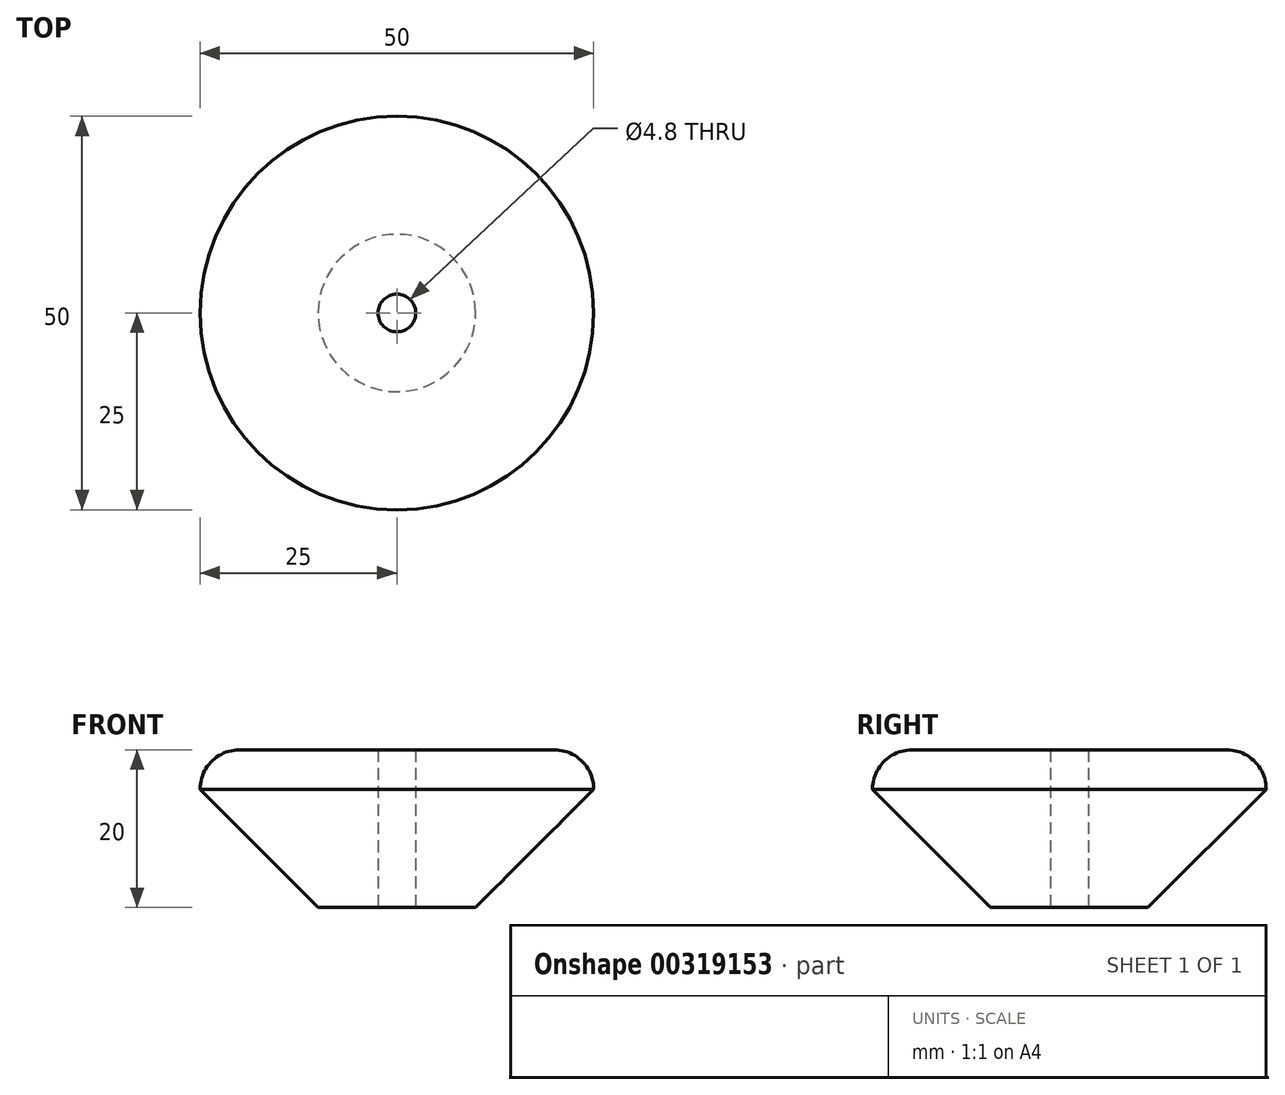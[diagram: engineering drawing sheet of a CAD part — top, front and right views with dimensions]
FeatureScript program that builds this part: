
annotation { "Feature Type Name" : "Feature", "Feature Type Description" : "" }
export const myFeature = defineFeature(function(context is Context, id is Id, definition is map)
    precondition{}
    {
        {
            var Q0;
            Q0=qCreatedBy(makeId("Top.planeOp"),FACE);
            var sketch = newSketch(context, id + "F0", { "sketchPlane" : qUnion([Q0])});
            skCircle(sketch, "E0", {"center": v(0, 0) * mm, "radius": 25 * mm});
            skCircle(sketch, "E1", {"center": v(0, 0) * mm, "radius": 2.4 * mm});
            skSolve(sketch);
        }
        {
            var Q0;
            Q0=qSketchRegion(id+"F0",true);
            var Q1;
            Q1=makeQuery(id+"F0.imprint","IMPRINT",FACE,{"disambiguationData":[TD([[makeQuery(id+"F0.imprint","IMPRINT",EDGE,{"derivedFrom":sQuery(id+"F0.wireOp",EDGE,"E0")}),1.0]])]});
            extrude(context, id + "F1", {"entities" : qUnion([Q0, Q1]), "depth" : 20 * mm});
        }
        {
            var Q0;
            Q0=makeQuery(id+"F1.opExtrude","CAP_EDGE",EDGE,{"disambiguationData":[OSD([sQuery(id+"F0.wireOp",EDGE,"E0")])],"isStart":true});
            chamfer(context, id + "F2", {"entities" : qUnion([Q0]), "width" : 15 * mm, "tangentPropagation" : true});
        }
        {
            var Q0;
            Q0=makeQuery(id+"F1.opExtrude","CAP_EDGE",EDGE,{"disambiguationData":[OSD([sQuery(id+"F0.wireOp",EDGE,"E0")])],"isStart":false});
            fillet(context, id + "F3", {"entities" : qUnion([Q0]), "radius" : 5 * mm, "tangentPropagation" : true, "allowEdgeOverflow" : false});
        }
    });
